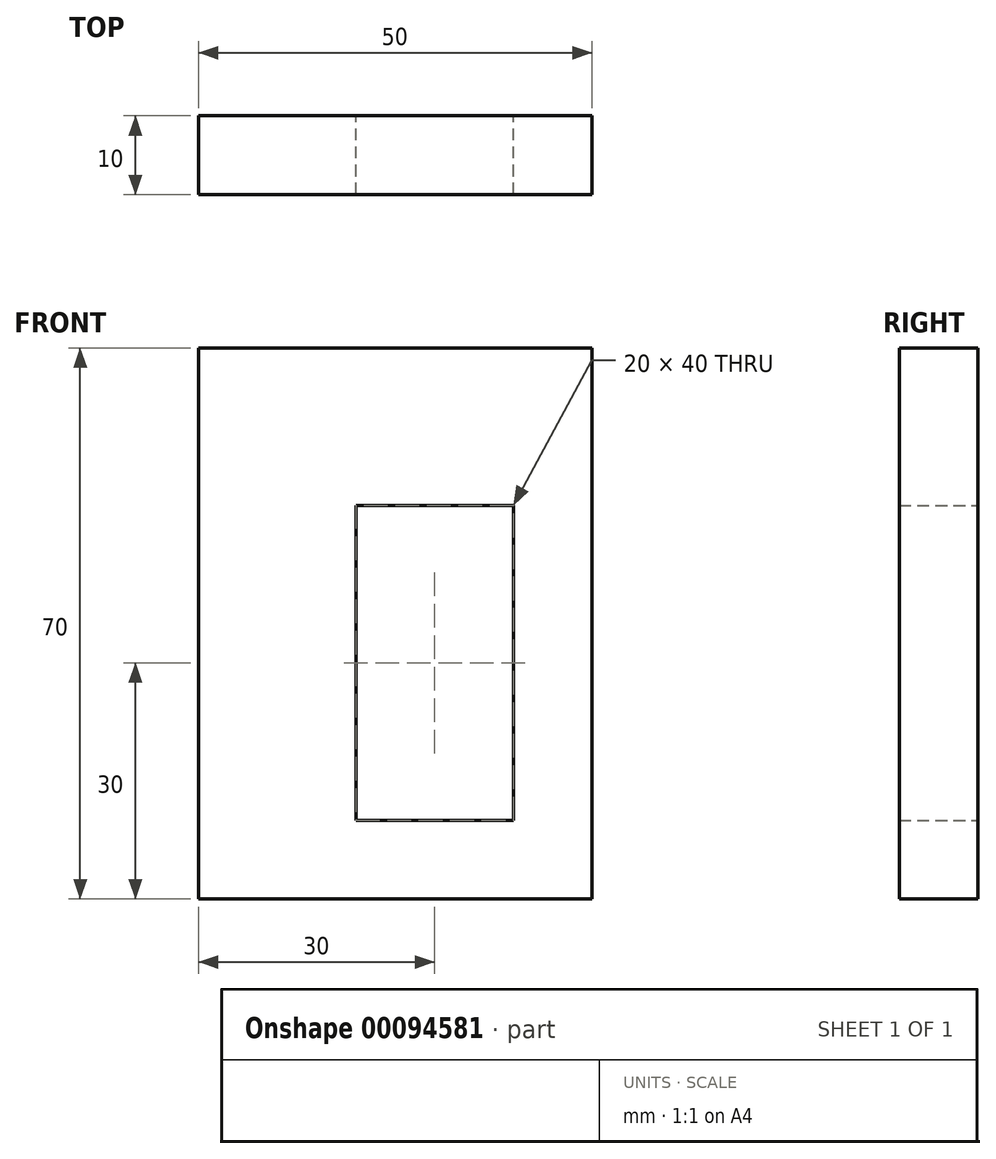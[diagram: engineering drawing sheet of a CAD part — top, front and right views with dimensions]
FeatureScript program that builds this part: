
annotation { "Feature Type Name" : "Feature", "Feature Type Description" : "" }
export const myFeature = defineFeature(function(context is Context, id is Id, definition is map)
    precondition{}
    {
        {
            var Q0;
            Q0=qCreatedBy(makeId("Front.planeOp"),FACE);
            var sketch = newSketch(context, id + "F0", { "sketchPlane" : qUnion([Q0])});
            skLineSegment(sketch, "E0", {"start": v(-20, 20) * mm, "end": v(30, 20) * mm});
            skLineSegment(sketch, "E1", {"start": v(30, 20) * mm, "end": v(30, -50) * mm});
            skLineSegment(sketch, "E2", {"start": v(30, -50) * mm, "end": v(-20, -50) * mm});
            skLineSegment(sketch, "E3", {"start": v(-20, -50) * mm, "end": v(-20, 20) * mm});
            skLineSegment(sketch, "E4", {"start": v(20, -40) * mm, "end": v(20, 0) * mm});
            skLineSegment(sketch, "E5", {"start": v(20, 0) * mm, "end": v(0, 0) * mm});
            skLineSegment(sketch, "E6", {"start": v(0, 0) * mm, "end": v(0, -40) * mm});
            skLineSegment(sketch, "E7", {"start": v(0, -40) * mm, "end": v(20, -40) * mm});
            skSolve(sketch);
        }
        {
            var Q0;
            Q0 = qSketchRegion(id + "F0", true);
            var Q1;
            Q1=makeQuery(id+"F0.imprint","IMPRINT",FACE,{"disambiguationData":[TD([[makeQuery(id+"F0.imprint","IMPRINT",EDGE,{"derivedFrom":sQuery(id+"F0.wireOp",EDGE,"E0")}),-1.0]])]});
            extrude(context, id + "F1", {"entities" : qUnion([Q0, Q1]), "depth" : 10 * mm});
        }
    });
